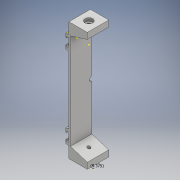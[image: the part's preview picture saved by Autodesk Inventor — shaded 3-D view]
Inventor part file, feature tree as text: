
AUTODESK INVENTOR PART (.ipt)
format: ipt  version: 2018 (Build 220112000, 112)  size: 769,024 bytes
history: native  units: mm
features: sketch x39, extrude x28, fillet x4, chamfer x2
ambient origin geometry x8: Origin, YZ Plane, XZ Plane, XY Plane, X Axis, Y Axis, Z Axis, Center Point
bodies: Solid1 (feature_tree)
feature tree (73):
  extrude  "Extrusion1"  Depth=125.0mm
  extrude  "Extrusion2"  Depth=2.0mm
  extrude  "Extrusion3"  Depth=2.0mm TaperAngle=0.0deg
  extrude  "Extrusion4"  Depth=7.1mm TaperAngle=0.0deg
  extrude  "Extrusion5"  Depth=155.0mm TaperAngle=0.0deg
  chamfer  "Chamfer1"  Distance=7.1mm
  sketch  "Sketch6"  dims[d16=22.0mm d17=7.1mm d18=0.0mm d19=7.0mm d20=2.0mm d21=12.61873mm]
  chamfer  "Chamfer2"  Distance=2.0mm
  sketch  "Sketch7"  dims[d22=7.0mm d23=2.0mm d24=12.61873mm d25=8.0mm]
  sketch  "Sketch8"  dims[d26=2.0mm d27=0.0mm d28=8.0mm]
  sketch  "Sketch9"  dims[d29=2.0mm d30=0.0mm d31=2.0mm d32=0.0mm]
  extrude  "Extrusion6"  Depth=2.0mm
  extrude  "Extrusion7"  Depth=2.0mm
  extrude  "Extrusion8"  Depth=2.0mm TaperAngle=0.0deg
  extrude  "Extrusion9"  Depth=2.0mm
  sketch  "Sketch13"  dims[d45=2.0mm d46=38.0mm]
  sketch  "Sketch14"  dims[d47=2.0mm d48=0.0mm d49=38.0mm]
  extrude  "Extrusion10"  Depth=2.0mm
  sketch  "Sketch16"  dims[d53=38.0mm d54=40.75mm]
  extrude  "Extrusion11"  Depth=2.0mm TaperAngle=0.0deg
  fillet  "Fillet1"  Radius=2.0mm
  fillet  "Fillet2"  Radius=2.0mm
  extrude  "Extrusion12"  Depth=2.0mm
  extrude  "Extrusion13"  Depth=2.0mm
  extrude  "Extrusion14"  Depth=21.75mm
  sketch  "Sketch21"  dims[d67=12.0mm d68=3.0mm]
  extrude  "Extrusion15"  Depth=40.75mm
  extrude  "Extrusion16"  Depth=40.75mm
  sketch  "Sketch24"  dims[d75=5.0mm d76=5.0mm]
  sketch  "Sketch25"  dims[d77=5.0mm d78=5.0mm]
  extrude  "Extrusion17"  Depth=32.0mm TaperAngle=0.0deg
  extrude  "Extrusion18"  Depth=12.0mm
  sketch  "Sketch28"  dims[d85=30.0mm d86=0.0mm d87=30.0mm d88=0.0mm]
  fillet  "Fillet3"  Radius=3.0mm
  extrude  "Extrusion19"  Depth=3.0mm
  extrude  "Extrusion20"  Depth=3.0mm
  sketch  "Sketch31"  dims[d96=10.0mm]
  extrude  "Extrusion21"  Depth=2.0mm
  extrude  "Extrusion22"  Depth=2.0mm TaperAngle=0.0deg
  extrude  "Extrusion23"  Depth=5.0mm
  extrude  "Extrusion24"  Depth=5.0mm
  extrude  "Extrusion25"  Depth=9.375mm
  extrude  "Extrusion26"  Depth=2.0mm TaperAngle=0.0deg
  extrude  "Extrusion27"  Depth=30.0mm TaperAngle=0.0deg
  extrude  "Extrusion28"  Depth=28.0mm TaperAngle=0.0deg
  fillet  "Fillet4"  Radius=4.0mm
  sketch  "Sketch1"  dims[d0=24.0mm d1=125.0mm]
  sketch  "Sketch2"  dims[d2=2.0mm d3=0.0mm d4=15.0mm]
  sketch  "Sketch3"  dims[d5=15.0mm d6=22.0mm d7=2.0mm d8=0.0mm d9=0.0mm]
  sketch  "Sketch4"  dims[d10=22.0mm d11=7.1mm d12=0.0mm]
  sketch  "Sketch5"  dims[d13=9.0mm d14=155.0mm d15=0.0mm]
  sketch  "Sketch10"  dims[d33=2.0mm d34=0.0mm d35=5.5mm]
  sketch  "Sketch11"  dims[d36=11.0mm d37=2.0mm]
  sketch  "Sketch12"  dims[d38=2.0mm d39=7.0mm d40=0.0mm d42=2.0mm d43=0.0mm d44=2.0mm]
  sketch  "Sketch15"  dims[d51=43.5mm d52=21.75mm]
  sketch  "Sketch17"  dims[d55=38.0mm d56=40.75mm]
  sketch  "Sketch18"  dims[d57=30.0mm d58=0.0mm d59=32.0mm d60=0.0mm]
  sketch  "Sketch19"  dims[d61=3.0mm d62=12.0mm d63=3.0mm]
  sketch  "Sketch20"  dims[d64=3.1mm d65=0.0mm d66=3.0mm]
  sketch  "Sketch22"  dims[d69=3.1mm d70=0.0mm d71=2.0mm]
  sketch  "Sketch23"  dims[d72=2.0mm d73=3.6mm d74=0.0mm]
  sketch  "Sketch26"  dims[d79=1.0mm d80=0.0mm d81=9.375mm]
  sketch  "Sketch27"  dims[d82=2.0mm d83=100.0mm d84=0.0mm]
  sketch  "Sketch29"  dims[d89=8.0mm d90=0.0mm d91=28.0mm d92=0.0mm d93=4.0mm]
  sketch  "Sketch30"  dims[d94=169.0mm d95=0.0mm]
  sketch  "Sketch32"  dims[d97=4.0mm d98=0.0mm]
  sketch  "Sketch33"  dims[d99=4.0mm d100=0.0mm]
  sketch  "Sketch34"  dims[d101=6.35mm]
  sketch  "Sketch35"  dims[d102=40.0mm d103=0.0mm]
  sketch  "Sketch36"  dims[d104=1.0mm]
  sketch  "Sketch37"  dims[d105=1.0mm]
  sketch  "Sketch38"  dims[d106=5.0mm d107=0.0mm]
  sketch  "Sketch39"  dims[d108=2.0mm]
